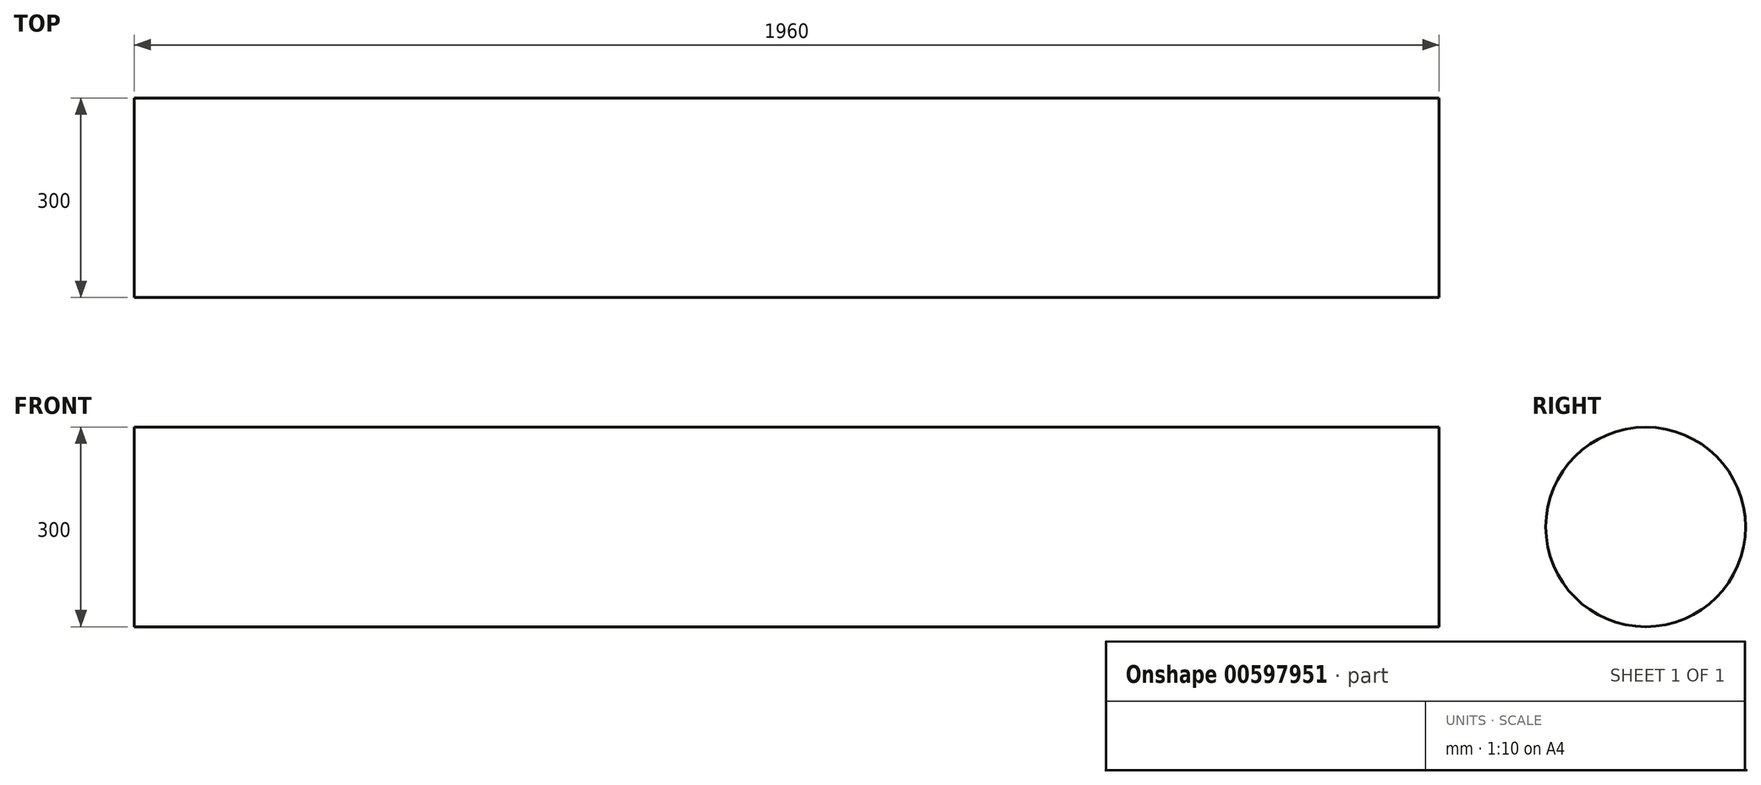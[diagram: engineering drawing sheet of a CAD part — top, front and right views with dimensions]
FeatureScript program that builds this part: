
annotation { "Feature Type Name" : "Feature", "Feature Type Description" : "" }
export const myFeature = defineFeature(function(context is Context, id is Id, definition is map)
    precondition{}
    {
        {
            var Q0;
            Q0=qCreatedBy(makeId("Right.planeOp"),FACE);
            var sketch = newSketch(context, id + "F0", { "sketchPlane" : qUnion([Q0])});
            skCircle(sketch, "E0", {"center": v(0, 0) * mm, "radius": 150 * mm});
            skSolve(sketch);
        }
        {
            var Q0;
            Q0 = qSketchRegion(id + "F0", true);
            extrude(context, id + "F1", {"entities" : qUnion([Q0]), "depth" : 1960 * mm, "offsetDistance" : 25 * mm});
        }
    });
